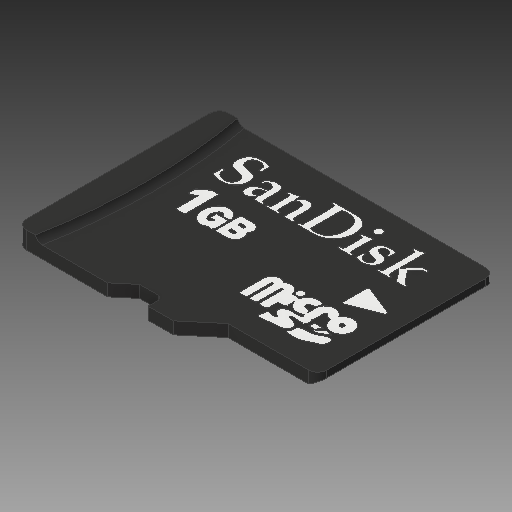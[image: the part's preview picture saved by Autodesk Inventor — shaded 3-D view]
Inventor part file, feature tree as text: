
AUTODESK INVENTOR PART (.ipt)
format: ipt  version: 2019.4 (Build 234330000, 330)  size: 901,120 bytes
history: native  units: in
note: dims shown in document units (in); Inventor stores cm internally (conversion verified against a paired STEP export)
features: chamfer x1
ambient origin geometry x8: Origin, YZ Plane, XZ Plane, XY Plane, X Axis, Y Axis, Z Axis, Center Point
bodies: Solid1 (feature_tree)
feature tree (1):
  chamfer  "Chamfer1"  [1 undecoded]
note: 1 required parameter value undecoded (feature->parameter linkage not recoverable at this tier; creation-order binding heuristic only, values carry confidence <= 0.55)
